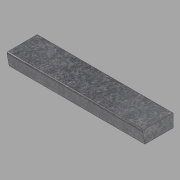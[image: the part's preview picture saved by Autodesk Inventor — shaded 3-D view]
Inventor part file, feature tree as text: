
AUTODESK INVENTOR PART (.ipt)
format: ipt  version: 2022.1 (Build 261234020, 234B)  size: 99,840 bytes
history: native  units: in
note: dims shown in document units (in); Inventor stores cm internally (conversion verified against a paired STEP export)
features: extrude x1, sketch x1
ambient origin geometry x8: Origin, YZ Plane, XZ Plane, XY Plane, X Axis, Y Axis, Z Axis, Center Point
bodies: Solid1 (feature_tree)
feature tree (2):
  extrude  "Extrusion1"  Depth=13.0in
  sketch  "Sketch2"  dims[d2=6.0in d3=13.0in d4=0.5in d5=62.8in d6=0.0in d7=13.5in]
